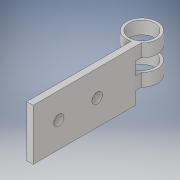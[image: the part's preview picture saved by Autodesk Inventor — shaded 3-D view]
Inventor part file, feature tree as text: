
AUTODESK INVENTOR PART (.ipt)
format: ipt  version: 2019 (Build 230136000, 136)  size: 142,848 bytes
history: native  units: in
note: dims shown in document units (in); Inventor stores cm internally (conversion verified against a paired STEP export)
features: extrude x5, sketch x5, plane x1
ambient origin geometry x8: Origin, YZ Plane, XZ Plane, XY Plane, X Axis, Y Axis, Z Axis, Center Point
bodies: Solid1 (feature_tree)
feature tree (11):
  extrude  "Extrusion1"  Depth=2.0in
  extrude  "Extrusion2"  Depth=0.125in
  plane  "Work Plane1"
  extrude  "Extrusion3"  Depth=0.25in
  extrude  "Extrusion4"  Depth=0.5in
  extrude  "Extrusion5"  Depth=0.5in
  sketch  "Sketch1"  dims[d0=1.0in d1=2.0in]
  sketch  "Sketch2"  dims[d2=0.125in d3=0.0in d4=0.6in]
  sketch  "Sketch3"  dims[d5=0.25in d6=0.0in d7=0.25in]
  sketch  "Sketch4"  dims[d8=0.25in d9=0.0in d10=0.5in]
  sketch  "Sketch5"  dims[d11=5.0in d12=0.0in d13=0.5in d14=0.75in d15=0.2031in d16=0.2031in d17=5.0in d18=0.0in]
